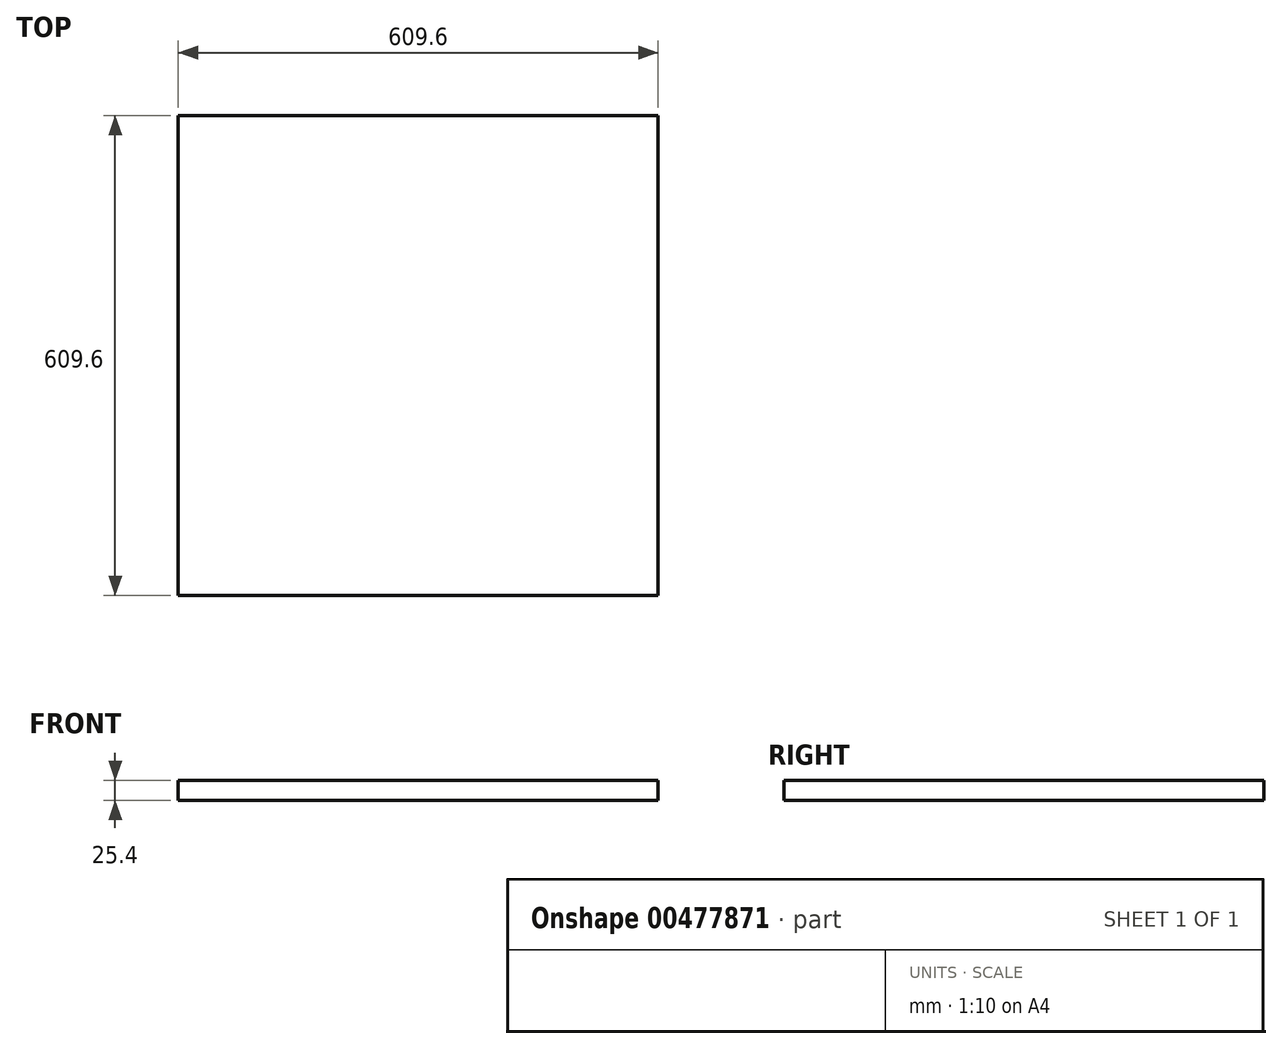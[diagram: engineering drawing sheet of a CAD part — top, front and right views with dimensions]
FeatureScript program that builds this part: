
annotation { "Feature Type Name" : "Feature", "Feature Type Description" : "" }
export const myFeature = defineFeature(function(context is Context, id is Id, definition is map)
    precondition{}
    {
        {
            var Q0;
            Q0=qCreatedBy(makeId("Top.planeOp"),FACE);
            var sketch = newSketch(context, id + "F0", { "sketchPlane" : qUnion([Q0])});
            skLineSegment(sketch, "E0.bottom", {"start": v(0, -602.73) * mm, "end": v(609.6, -602.73) * mm});
            skLineSegment(sketch, "E0.top", {"start": v(0, 6.87) * mm, "end": v(609.6, 6.87) * mm});
            skLineSegment(sketch, "E0.left", {"start": v(0, -602.73) * mm, "end": v(0, 6.87) * mm});
            skLineSegment(sketch, "E0.right", {"start": v(609.6, -602.73) * mm, "end": v(609.6, 6.87) * mm});
            skSolve(sketch);
        }
        {
            var Q0;
            Q0=makeQuery(id+"F0.imprint","IMPRINT",FACE,{"disambiguationData":[TD([[makeQuery(id+"F0.imprint","IMPRINT",EDGE,{"derivedFrom":sQuery(id+"F0.wireOp",EDGE,"E0.bottom")}),1.0]])]});
            extrude(context, id + "F1", {"entities" : qUnion([Q0]), "depth" : 25.4 * mm, "offsetDistance" : 25.4 * mm});
        }
    });
